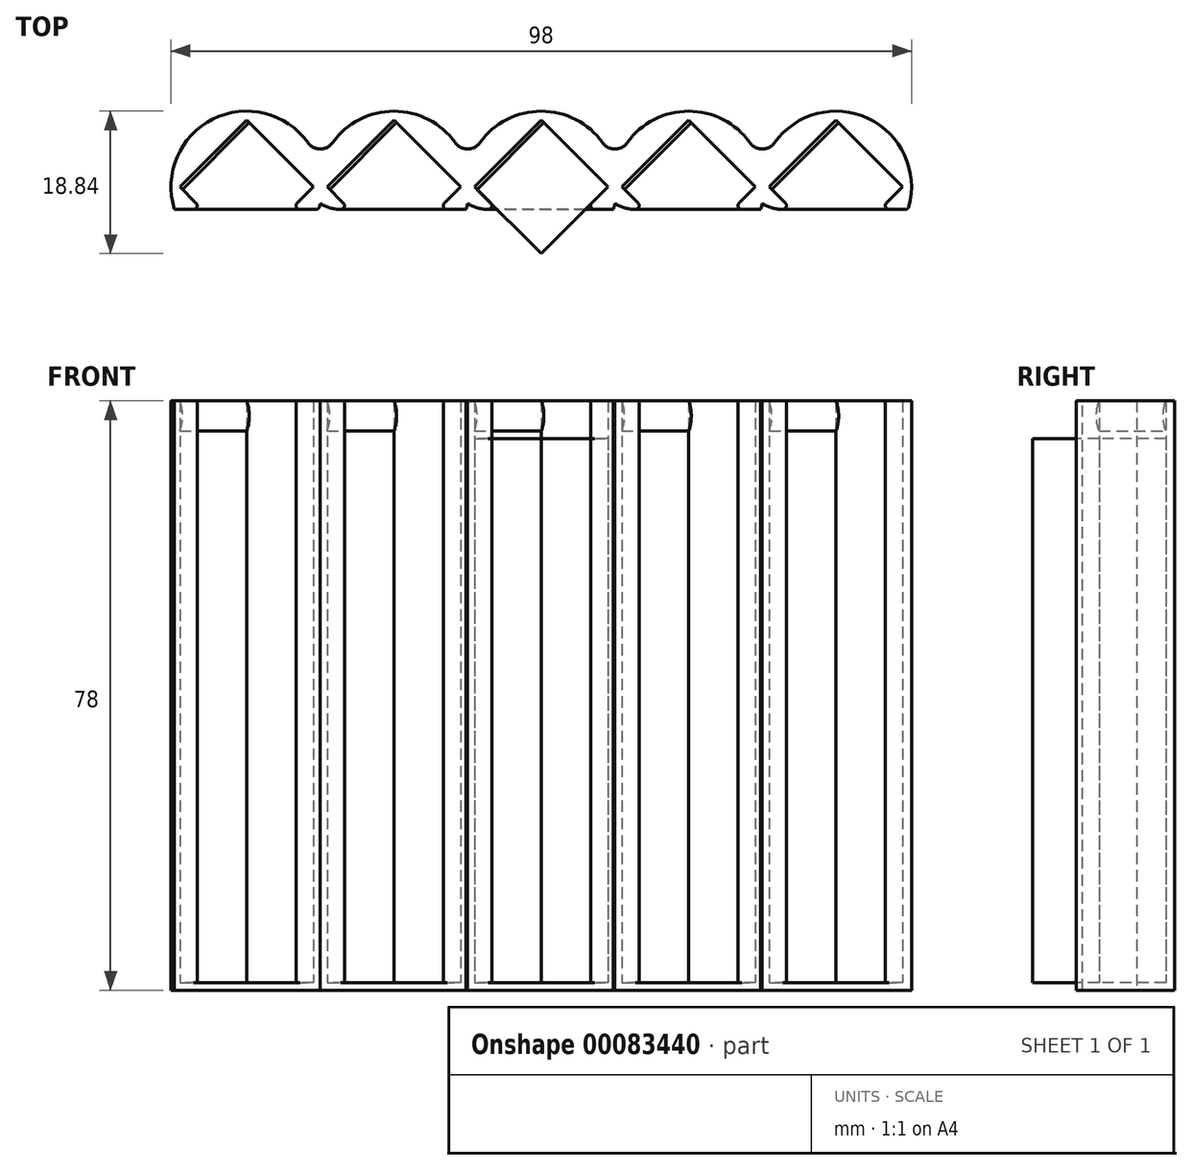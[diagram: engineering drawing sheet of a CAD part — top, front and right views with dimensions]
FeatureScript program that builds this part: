
annotation { "Feature Type Name" : "Feature", "Feature Type Description" : "" }
export const myFeature = defineFeature(function(context is Context, id is Id, definition is map)
    precondition{}
    {
        {
            assignVariable(context, id + "F0", {"name" : "dieSize", "anyValue" : 12.5});
        }
        {
            var Q0;
            Q0=qCreatedBy(makeId("Top.planeOp"),FACE);
            var sketch = newSketch(context, id + "F1", { "sketchPlane" : qUnion([Q0])});
            skCircle(sketch, "E0", {"center": v(0, 0) * mm, "radius": 10 * mm});
            skLineSegment(sketch, "E1", {"start": v(0, 0) * mm, "end": v(0, 26.13) * mm, "construction": true});
            skLineSegment(sketch, "E2", {"start": v(0, 8.84) * mm, "end": v(-8.84, 0) * mm});
            skLineSegment(sketch, "E3", {"start": v(0, 8.84) * mm, "end": v(8.84, 0) * mm});
            skLineSegment(sketch, "E4", {"start": v(8.84, 0) * mm, "end": v(0, -8.84) * mm});
            skLineSegment(sketch, "E5", {"start": v(-8.84, 0) * mm, "end": v(0, -8.84) * mm});
            skLineSegment(sketch, "E6", {"start": v(0, 0) * mm, "end": v(18.44, -18.44) * mm, "construction": true});
            skLineSegment(sketch, "E7", {"start": v(0, 0) * mm, "end": v(-23.78, 0) * mm, "construction": true});
            skLineSegment(sketch, "E8.1.0.0", {"start": v(28.34, 0) * mm, "end": v(19.5, -8.84) * mm});
            skLineSegment(sketch, "E8.1.0.1", {"start": v(19.5, 8.84) * mm, "end": v(28.34, 0) * mm});
            skLineSegment(sketch, "E8.1.0.2", {"start": v(10.66, 0) * mm, "end": v(19.5, -8.84) * mm});
            skCircle(sketch, "E8.1.0.3", {"center": v(19.5, 0) * mm, "radius": 10 * mm});
            skLineSegment(sketch, "E8.1.0.4", {"start": v(19.5, 8.84) * mm, "end": v(10.66, 0) * mm});
            skLineSegment(sketch, "E8.2.0.0", {"start": v(47.84, 0) * mm, "end": v(39, -8.84) * mm});
            skLineSegment(sketch, "E8.2.0.1", {"start": v(39, 8.84) * mm, "end": v(47.84, 0) * mm});
            skLineSegment(sketch, "E8.2.0.2", {"start": v(30.16, 0) * mm, "end": v(39, -8.84) * mm});
            skCircle(sketch, "E8.2.0.3", {"center": v(39, 0) * mm, "radius": 10 * mm});
            skLineSegment(sketch, "E8.2.0.4", {"start": v(39, 8.84) * mm, "end": v(30.16, 0) * mm});
            skLineSegment(sketch, "E8.3.0.0", {"start": v(67.34, 0) * mm, "end": v(58.5, -8.84) * mm});
            skLineSegment(sketch, "E8.3.0.1", {"start": v(58.5, 8.84) * mm, "end": v(67.34, 0) * mm});
            skLineSegment(sketch, "E8.3.0.2", {"start": v(49.66, 0) * mm, "end": v(58.5, -8.84) * mm});
            skCircle(sketch, "E8.3.0.3", {"center": v(58.5, 0) * mm, "radius": 10 * mm});
            skLineSegment(sketch, "E8.3.0.4", {"start": v(58.5, 8.84) * mm, "end": v(49.66, 0) * mm});
            skLineSegment(sketch, "E8.4.0.0", {"start": v(86.84, 0) * mm, "end": v(78, -8.84) * mm});
            skLineSegment(sketch, "E8.4.0.1", {"start": v(78, 8.84) * mm, "end": v(86.84, 0) * mm});
            skLineSegment(sketch, "E8.4.0.2", {"start": v(69.16, 0) * mm, "end": v(78, -8.84) * mm});
            skCircle(sketch, "E8.4.0.3", {"center": v(78, 0) * mm, "radius": 10 * mm});
            skLineSegment(sketch, "E8.4.0.4", {"start": v(78, 8.84) * mm, "end": v(69.16, 0) * mm});
            skLineSegment(sketch, "E8.direction1", {"start": v(0, -8.84) * mm, "end": v(19.5, -8.84) * mm, "construction": true});
            skSolve(sketch);
        }
        {
            var Q0;
            Q0=makeQuery(id+"F1.imprint","IMPRINT",FACE,{"disambiguationData":[TD([[makeQuery(id+"F1.imprint","IMPRINT",EDGE,{"derivedFrom":sQuery(id+"F1.wireOp",EDGE,"E0")}),1.0]])]});
            var Q1;
            Q1=makeQuery(id+"F1.imprint","IMPRINT",FACE,{"disambiguationData":[TD([[makeQuery(id+"F1.imprint","IMPRINT",EDGE,{"derivedFrom":sQuery(id+"F1.wireOp",EDGE,"E8.1.0.0")}),1.0]])]});
            var Q2;
            Q2=makeQuery(id+"F1.imprint","IMPRINT",FACE,{"disambiguationData":[TD([[makeQuery(id+"F1.imprint","IMPRINT",EDGE,{"derivedFrom":sQuery(id+"F1.wireOp",EDGE,"E2")}),1.0]])]});
            var Q3;
            Q3=makeQuery(id+"F1.imprint","IMPRINT",FACE,{"disambiguationData":[TD([[makeQuery(id+"F1.imprint","IMPRINT",EDGE,{"derivedFrom":sQuery(id+"F1.wireOp",EDGE,"E8.1.0.0")}),-1.0]])]});
            var Q4;
            Q4=makeQuery(id+"F1.imprint","IMPRINT",FACE,{"disambiguationData":[TD([[makeQuery(id+"F1.imprint","IMPRINT",EDGE,{"derivedFrom":sQuery(id+"F1.wireOp",EDGE,"E8.2.0.0")}),-1.0]])]});
            var Q5;
            Q5=makeQuery(id+"F1.imprint","IMPRINT",FACE,{"disambiguationData":[TD([[makeQuery(id+"F1.imprint","IMPRINT",EDGE,{"derivedFrom":sQuery(id+"F1.wireOp",EDGE,"E8.3.0.0")}),-1.0]])]});
            var Q6;
            Q6=makeQuery(id+"F1.imprint","IMPRINT",FACE,{"disambiguationData":[TD([[makeQuery(id+"F1.imprint","IMPRINT",EDGE,{"derivedFrom":sQuery(id+"F1.wireOp",EDGE,"E8.4.0.0")}),-1.0]])]});
            var Q7;
            Q7=makeQuery(id+"F1.imprint","IMPRINT",FACE,{"disambiguationData":[TD([[makeQuery(id+"F1.imprint","IMPRINT",EDGE,{"derivedFrom":sQuery(id+"F1.wireOp",EDGE,"E2")}),-1.0]])]});
            var Q8;
            {var subQ0=sQuery(id+"F1.wireOp",EDGE,"E8.2.0.3");var subQ1=sQuery(id+"F1.wireOp",EDGE,"E8.1.0.3");var subQ2=makeQuery(id+"F1.imprint","INTERSECT",VERTEX,{"disambiguationData":[OD(0.0)],"derivedFrom":[subQ1,subQ0]});Q8=makeQuery(id+"F1.imprint","IMPRINT",FACE,{"disambiguationData":[TD([[makeQuery(id+"F1.imprint","IMPRINT",EDGE,{"disambiguationData":[TD([[subQ2,1.0]])],"derivedFrom":subQ1}),1.0]])]});}
            var Q9;
            Q9=makeQuery(id+"F1.imprint","IMPRINT",FACE,{"disambiguationData":[TD([[makeQuery(id+"F1.imprint","IMPRINT",EDGE,{"derivedFrom":sQuery(id+"F1.wireOp",EDGE,"E8.2.0.0")}),1.0]])]});
            var Q10;
            {var subQ0=sQuery(id+"F1.wireOp",EDGE,"E8.3.0.3");var subQ1=sQuery(id+"F1.wireOp",EDGE,"E8.2.0.3");var subQ2=makeQuery(id+"F1.imprint","INTERSECT",VERTEX,{"disambiguationData":[OD(0.0)],"derivedFrom":[subQ1,subQ0]});Q10=makeQuery(id+"F1.imprint","IMPRINT",FACE,{"disambiguationData":[TD([[makeQuery(id+"F1.imprint","IMPRINT",EDGE,{"disambiguationData":[TD([[subQ2,1.0]])],"derivedFrom":subQ1}),1.0]])]});}
            var Q11;
            Q11=makeQuery(id+"F1.imprint","IMPRINT",FACE,{"disambiguationData":[TD([[makeQuery(id+"F1.imprint","IMPRINT",EDGE,{"derivedFrom":sQuery(id+"F1.wireOp",EDGE,"E8.4.0.0")}),1.0]])]});
            var Q12;
            {var subQ0=sQuery(id+"F1.wireOp",EDGE,"E8.4.0.3");var subQ1=sQuery(id+"F1.wireOp",EDGE,"E8.3.0.3");var subQ2=makeQuery(id+"F1.imprint","INTERSECT",VERTEX,{"disambiguationData":[OD(0.0)],"derivedFrom":[subQ1,subQ0]});Q12=makeQuery(id+"F1.imprint","IMPRINT",FACE,{"disambiguationData":[TD([[makeQuery(id+"F1.imprint","IMPRINT",EDGE,{"disambiguationData":[TD([[subQ2,1.0]])],"derivedFrom":subQ1}),1.0]])]});}
            var Q13;
            Q13=makeQuery(id+"F1.imprint","IMPRINT",FACE,{"disambiguationData":[TD([[makeQuery(id+"F1.imprint","IMPRINT",EDGE,{"derivedFrom":sQuery(id+"F1.wireOp",EDGE,"E8.3.0.0")}),1.0]])]});
            extrude(context, id + "F2", {"entities" : qUnion([Q0, Q1, Q2, Q3, Q4, Q5, Q6, Q7, Q8, Q9, Q10, Q11, Q12, Q13]), "oppositeDirection" : true, "depth" : 1 * mm});
        }
        {
            var Q0;
            Q0=makeQuery(id+"F1.imprint","IMPRINT",FACE,{"disambiguationData":[TD([[makeQuery(id+"F1.imprint","IMPRINT",EDGE,{"derivedFrom":sQuery(id+"F1.wireOp",EDGE,"E8.2.0.0")}),1.0]])]});
            var Q1;
            {var subQ0=sQuery(id+"F1.wireOp",EDGE,"E8.3.0.3");var subQ1=sQuery(id+"F1.wireOp",EDGE,"E8.2.0.3");var subQ2=makeQuery(id+"F1.imprint","INTERSECT",VERTEX,{"disambiguationData":[OD(0.0)],"derivedFrom":[subQ1,subQ0]});Q1=makeQuery(id+"F1.imprint","IMPRINT",FACE,{"disambiguationData":[TD([[makeQuery(id+"F1.imprint","IMPRINT",EDGE,{"disambiguationData":[TD([[subQ2,1.0]])],"derivedFrom":subQ1}),1.0]])]});}
            var Q2;
            {var subQ0=sQuery(id+"F1.wireOp",EDGE,"E8.2.0.3");var subQ1=sQuery(id+"F1.wireOp",EDGE,"E8.1.0.3");var subQ2=makeQuery(id+"F1.imprint","INTERSECT",VERTEX,{"disambiguationData":[OD(0.0)],"derivedFrom":[subQ1,subQ0]});Q2=makeQuery(id+"F1.imprint","IMPRINT",FACE,{"disambiguationData":[TD([[makeQuery(id+"F1.imprint","IMPRINT",EDGE,{"disambiguationData":[TD([[subQ2,1.0]])],"derivedFrom":subQ1}),1.0]])]});}
            var Q3;
            {var subQ0=sQuery(id+"F1.wireOp",EDGE,"E8.1.0.3");var subQ1=sQuery(id+"F1.wireOp",EDGE,"E0");var subQ2=makeQuery(id+"F1.imprint","INTERSECT",VERTEX,{"disambiguationData":[OD(0.0)],"derivedFrom":[subQ1,subQ0]});Q3=makeQuery(id+"F1.imprint","IMPRINT",FACE,{"disambiguationData":[TD([[makeQuery(id+"F1.imprint","IMPRINT",EDGE,{"disambiguationData":[TD([[subQ2,1.0]])],"derivedFrom":subQ1}),1.0]])]});}
            var Q4;
            Q4=makeQuery(id+"F1.imprint","IMPRINT",FACE,{"disambiguationData":[TD([[makeQuery(id+"F1.imprint","IMPRINT",EDGE,{"derivedFrom":sQuery(id+"F1.wireOp",EDGE,"E8.1.0.0")}),1.0]])]});
            var Q5;
            Q5=makeQuery(id+"F1.imprint","IMPRINT",FACE,{"disambiguationData":[TD([[makeQuery(id+"F1.imprint","IMPRINT",EDGE,{"derivedFrom":sQuery(id+"F1.wireOp",EDGE,"E2")}),-1.0]])]});
            var Q6;
            Q6=makeQuery(id+"F1.imprint","IMPRINT",FACE,{"disambiguationData":[TD([[makeQuery(id+"F1.imprint","IMPRINT",EDGE,{"derivedFrom":sQuery(id+"F1.wireOp",EDGE,"E8.3.0.0")}),1.0]])]});
            var Q7;
            {var subQ0=sQuery(id+"F1.wireOp",EDGE,"E8.4.0.3");var subQ1=sQuery(id+"F1.wireOp",EDGE,"E8.3.0.3");var subQ2=makeQuery(id+"F1.imprint","INTERSECT",VERTEX,{"disambiguationData":[OD(0.0)],"derivedFrom":[subQ1,subQ0]});Q7=makeQuery(id+"F1.imprint","IMPRINT",FACE,{"disambiguationData":[TD([[makeQuery(id+"F1.imprint","IMPRINT",EDGE,{"disambiguationData":[TD([[subQ2,1.0]])],"derivedFrom":subQ1}),1.0]])]});}
            var Q8;
            Q8=makeQuery(id+"F1.imprint","IMPRINT",FACE,{"disambiguationData":[TD([[makeQuery(id+"F1.imprint","IMPRINT",EDGE,{"derivedFrom":sQuery(id+"F1.wireOp",EDGE,"E8.4.0.0")}),1.0]])]});
            extrude(context, id + "F3", {"entities" : qUnion([Q0, Q1, Q2, Q3, Q4, Q5, Q6, Q7, Q8]), "operationType" : NewBodyOperationType.ADD, "depth" : (getVariable(context, 'dieSize') * 6 + 2) * mm});
        }
        {
            var Q0;
            Q0=makeQuery(id+"F3.opExtrude","CAP_FACE",FACE,{"disambiguationData":[OSD([sQuery(id+"F1.wireOp",EDGE,"E0"),sQuery(id+"F1.wireOp",EDGE,"E2"),sQuery(id+"F1.wireOp",EDGE,"E3"),sQuery(id+"F1.wireOp",EDGE,"E4"),sQuery(id+"F1.wireOp",EDGE,"E5"),sQuery(id+"F1.wireOp",EDGE,"E8.1.0.0"),sQuery(id+"F1.wireOp",EDGE,"E8.1.0.1"),sQuery(id+"F1.wireOp",EDGE,"E8.1.0.2"),sQuery(id+"F1.wireOp",EDGE,"E8.1.0.3"),sQuery(id+"F1.wireOp",EDGE,"E8.1.0.4"),sQuery(id+"F1.wireOp",EDGE,"E8.2.0.0"),sQuery(id+"F1.wireOp",EDGE,"E8.2.0.1"),sQuery(id+"F1.wireOp",EDGE,"E8.2.0.2"),sQuery(id+"F1.wireOp",EDGE,"E8.2.0.3"),sQuery(id+"F1.wireOp",EDGE,"E8.2.0.4"),sQuery(id+"F1.wireOp",EDGE,"E8.3.0.0"),sQuery(id+"F1.wireOp",EDGE,"E8.3.0.1"),sQuery(id+"F1.wireOp",EDGE,"E8.3.0.2"),sQuery(id+"F1.wireOp",EDGE,"E8.3.0.3"),sQuery(id+"F1.wireOp",EDGE,"E8.3.0.4"),sQuery(id+"F1.wireOp",EDGE,"E8.4.0.0"),sQuery(id+"F1.wireOp",EDGE,"E8.4.0.1"),sQuery(id+"F1.wireOp",EDGE,"E8.4.0.2"),sQuery(id+"F1.wireOp",EDGE,"E8.4.0.3"),sQuery(id+"F1.wireOp",EDGE,"E8.4.0.4")])],"isStart":false});
            var sketch = newSketch(context, id + "F4", { "sketchPlane" : qUnion([Q0])});
            skLineSegment(sketch, "E9.bottom", {"start": v(90.34, -3) * mm, "end": v(-15.54, -3) * mm});
            skLineSegment(sketch, "E9.top", {"start": v(90.34, -14.24) * mm, "end": v(-15.54, -14.24) * mm});
            skLineSegment(sketch, "E9.left", {"start": v(90.34, -3) * mm, "end": v(90.34, -14.24) * mm});
            skLineSegment(sketch, "E9.right", {"start": v(-15.54, -3) * mm, "end": v(-15.54, -14.24) * mm});
            skSolve(sketch);
        }
        {
            var Q0;
            {var subQ3=sQuery(id+"F4.wireOp",EDGE,"E9.bottom");var subQ5=makeQuery(id+"F3.opExtrude","CAP_EDGE",EDGE,{"disambiguationData":[OSD([sQuery(id+"F1.wireOp",EDGE,"E0")])],"isStart":false});var subQ7=makeQuery(id+"F4.imprint","INTERSECT",VERTEX,{"disambiguationData":[OD(1.0)],"derivedFrom":[subQ5,subQ3]});Q0=makeQuery(id+"F4.imprint","IMPRINT",FACE,{"disambiguationData":[TD([[makeQuery(id+"F4.imprint","IMPRINT",EDGE,{"disambiguationData":[TD([[subQ7,-1.0]])],"derivedFrom":subQ3}),1.0]])]});}
            var Q1;
            {var subQ0=sQuery(id+"F4.wireOp",EDGE,"E9.bottom");var subQ1=makeQuery(id+"F3.opExtrude","CAP_EDGE",EDGE,{"disambiguationData":[OSD([sQuery(id+"F1.wireOp",EDGE,"E4")])],"isStart":false});var subQ2=makeQuery(id+"F4.imprint","INTERSECT",VERTEX,{"derivedFrom":[subQ1,subQ0]});Q1=makeQuery(id+"F4.imprint","IMPRINT",FACE,{"disambiguationData":[TD([[makeQuery(id+"F4.imprint","IMPRINT",EDGE,{"disambiguationData":[TD([[subQ2,-1.0]])],"derivedFrom":subQ0}),1.0]])]});}
            var Q2;
            {var subQ0=makeQuery(id+"F3.opExtrude","CAP_EDGE",EDGE,{"disambiguationData":[OSD([sQuery(id+"F1.wireOp",EDGE,"E8.1.0.2")])],"isStart":false});var subQ1=makeQuery(id+"F3.opExtrude","CAP_EDGE",EDGE,{"disambiguationData":[OSD([sQuery(id+"F1.wireOp",EDGE,"E8.1.0.0")])],"isStart":false});var subQ2=makeQuery(id+"F4.imprint","INTERSECT",VERTEX,{"derivedFrom":[subQ1,subQ0]});Q2=makeQuery(id+"F4.imprint","IMPRINT",FACE,{"disambiguationData":[TD([[makeQuery(id+"F4.imprint","IMPRINT",EDGE,{"disambiguationData":[TD([[subQ2,1.0]])],"derivedFrom":subQ1}),1.0]])]});}
            var Q3;
            {var subQ0=sQuery(id+"F4.wireOp",EDGE,"E9.bottom");var subQ1=makeQuery(id+"F3.opExtrude","CAP_EDGE",EDGE,{"disambiguationData":[OSD([sQuery(id+"F1.wireOp",EDGE,"E8.1.0.0")])],"isStart":false});var subQ2=makeQuery(id+"F4.imprint","INTERSECT",VERTEX,{"derivedFrom":[subQ1,subQ0]});Q3=makeQuery(id+"F4.imprint","IMPRINT",FACE,{"disambiguationData":[TD([[makeQuery(id+"F4.imprint","IMPRINT",EDGE,{"disambiguationData":[TD([[subQ2,-1.0]])],"derivedFrom":subQ0}),1.0]])]});}
            var Q4;
            {var subQ0=makeQuery(id+"F3.opExtrude","CAP_EDGE",EDGE,{"disambiguationData":[OSD([sQuery(id+"F1.wireOp",EDGE,"E8.2.0.2")])],"isStart":false});var subQ1=makeQuery(id+"F3.opExtrude","CAP_EDGE",EDGE,{"disambiguationData":[OSD([sQuery(id+"F1.wireOp",EDGE,"E8.2.0.0")])],"isStart":false});var subQ2=makeQuery(id+"F4.imprint","INTERSECT",VERTEX,{"derivedFrom":[subQ1,subQ0]});Q4=makeQuery(id+"F4.imprint","IMPRINT",FACE,{"disambiguationData":[TD([[makeQuery(id+"F4.imprint","IMPRINT",EDGE,{"disambiguationData":[TD([[subQ2,1.0]])],"derivedFrom":subQ1}),1.0]])]});}
            var Q5;
            {var subQ0=sQuery(id+"F4.wireOp",EDGE,"E9.bottom");var subQ1=makeQuery(id+"F3.opExtrude","CAP_EDGE",EDGE,{"disambiguationData":[OSD([sQuery(id+"F1.wireOp",EDGE,"E8.2.0.0")])],"isStart":false});var subQ2=makeQuery(id+"F4.imprint","INTERSECT",VERTEX,{"derivedFrom":[subQ1,subQ0]});Q5=makeQuery(id+"F4.imprint","IMPRINT",FACE,{"disambiguationData":[TD([[makeQuery(id+"F4.imprint","IMPRINT",EDGE,{"disambiguationData":[TD([[subQ2,-1.0]])],"derivedFrom":subQ0}),1.0]])]});}
            var Q6;
            {var subQ0=makeQuery(id+"F3.opExtrude","CAP_EDGE",EDGE,{"disambiguationData":[OSD([sQuery(id+"F1.wireOp",EDGE,"E8.3.0.2")])],"isStart":false});var subQ1=makeQuery(id+"F3.opExtrude","CAP_EDGE",EDGE,{"disambiguationData":[OSD([sQuery(id+"F1.wireOp",EDGE,"E8.3.0.0")])],"isStart":false});var subQ2=makeQuery(id+"F4.imprint","INTERSECT",VERTEX,{"derivedFrom":[subQ1,subQ0]});Q6=makeQuery(id+"F4.imprint","IMPRINT",FACE,{"disambiguationData":[TD([[makeQuery(id+"F4.imprint","IMPRINT",EDGE,{"disambiguationData":[TD([[subQ2,1.0]])],"derivedFrom":subQ1}),1.0]])]});}
            var Q7;
            {var subQ0=sQuery(id+"F4.wireOp",EDGE,"E9.bottom");var subQ1=makeQuery(id+"F3.opExtrude","CAP_EDGE",EDGE,{"disambiguationData":[OSD([sQuery(id+"F1.wireOp",EDGE,"E8.3.0.0")])],"isStart":false});var subQ2=makeQuery(id+"F4.imprint","INTERSECT",VERTEX,{"derivedFrom":[subQ1,subQ0]});Q7=makeQuery(id+"F4.imprint","IMPRINT",FACE,{"disambiguationData":[TD([[makeQuery(id+"F4.imprint","IMPRINT",EDGE,{"disambiguationData":[TD([[subQ2,-1.0]])],"derivedFrom":subQ0}),1.0]])]});}
            var Q8;
            {var subQ3=sQuery(id+"F4.wireOp",EDGE,"E9.bottom");var subQ6=makeQuery(id+"F3.opExtrude","CAP_EDGE",EDGE,{"disambiguationData":[OSD([sQuery(id+"F1.wireOp",EDGE,"E8.4.0.3")])],"isStart":false});var subQ8=makeQuery(id+"F4.imprint","INTERSECT",VERTEX,{"disambiguationData":[OD(0.0)],"derivedFrom":[subQ6,subQ3]});Q8=makeQuery(id+"F4.imprint","IMPRINT",FACE,{"disambiguationData":[TD([[makeQuery(id+"F4.imprint","IMPRINT",EDGE,{"disambiguationData":[TD([[subQ8,-1.0]])],"derivedFrom":subQ3}),1.0]])]});}
            var Q9;
            {var subQ0=sQuery(id+"F4.wireOp",EDGE,"E9.bottom");var subQ1=makeQuery(id+"F3.opExtrude","CAP_EDGE",EDGE,{"disambiguationData":[OSD([sQuery(id+"F1.wireOp",EDGE,"E8.4.0.0")])],"isStart":false});var subQ2=makeQuery(id+"F4.imprint","INTERSECT",VERTEX,{"derivedFrom":[subQ1,subQ0]});Q9=makeQuery(id+"F4.imprint","IMPRINT",FACE,{"disambiguationData":[TD([[makeQuery(id+"F4.imprint","IMPRINT",EDGE,{"disambiguationData":[TD([[subQ2,-1.0]])],"derivedFrom":subQ0}),1.0]])]});}
            var Q10;
            Q10=makeQuery(id+"F2.opExtrude","CAP_FACE",FACE,{"disambiguationData":[OSD([sQuery(id+"F1.wireOp",EDGE,"E0"),sQuery(id+"F1.wireOp",EDGE,"E8.1.0.3"),sQuery(id+"F1.wireOp",EDGE,"E8.2.0.3"),sQuery(id+"F1.wireOp",EDGE,"E8.3.0.3"),sQuery(id+"F1.wireOp",EDGE,"E8.4.0.3")])],"isStart":false});
            extrude(context, id + "F5", {"entities" : qUnion([Q0, Q1, Q2, Q3, Q4, Q5, Q6, Q7, Q8, Q9]), "operationType" : NewBodyOperationType.REMOVE, "endBound" : BoundingType.UP_TO_SURFACE, "oppositeDirection" : true, "endBoundEntityFace" : qUnion([Q10]), "depth" : 25 * mm});
        }
        {
            var Q0;
            {var subQ0=sQuery(id+"F1.wireOp",EDGE,"E8.4.0.3");var subQ1=sQuery(id+"F1.wireOp",EDGE,"E8.3.0.3");var subQ2=makeQuery(id+"F1.imprint","INTERSECT",VERTEX,{"disambiguationData":[OD(0.0)],"derivedFrom":[subQ1,subQ0]});Q0=makeQuery(id+"F3.boolean.opBoolean","MERGE",EDGE,{"derivedFrom":[makeQuery(id+"F2.opExtrude","SWEPT_EDGE",EDGE,{"disambiguationData":[OSD([subQ1,subQ0]),TDD([subQ2])]}),makeQuery(id+"F3.opExtrude","SWEPT_EDGE",EDGE,{"disambiguationData":[OSD([subQ1,subQ0]),TDD([subQ2])]})]});}
            var Q1;
            {var subQ0=sQuery(id+"F1.wireOp",EDGE,"E8.3.0.3");var subQ1=sQuery(id+"F1.wireOp",EDGE,"E8.2.0.3");var subQ2=makeQuery(id+"F1.imprint","INTERSECT",VERTEX,{"disambiguationData":[OD(0.0)],"derivedFrom":[subQ1,subQ0]});Q1=makeQuery(id+"F3.boolean.opBoolean","MERGE",EDGE,{"derivedFrom":[makeQuery(id+"F2.opExtrude","SWEPT_EDGE",EDGE,{"disambiguationData":[OSD([subQ1,subQ0]),TDD([subQ2])]}),makeQuery(id+"F3.opExtrude","SWEPT_EDGE",EDGE,{"disambiguationData":[OSD([subQ1,subQ0]),TDD([subQ2])]})]});}
            var Q2;
            {var subQ0=sQuery(id+"F1.wireOp",EDGE,"E8.2.0.3");var subQ1=sQuery(id+"F1.wireOp",EDGE,"E8.1.0.3");var subQ2=makeQuery(id+"F1.imprint","INTERSECT",VERTEX,{"disambiguationData":[OD(0.0)],"derivedFrom":[subQ1,subQ0]});Q2=makeQuery(id+"F3.boolean.opBoolean","MERGE",EDGE,{"derivedFrom":[makeQuery(id+"F2.opExtrude","SWEPT_EDGE",EDGE,{"disambiguationData":[OSD([subQ1,subQ0]),TDD([subQ2])]}),makeQuery(id+"F3.opExtrude","SWEPT_EDGE",EDGE,{"disambiguationData":[OSD([subQ1,subQ0]),TDD([subQ2])]})]});}
            var Q3;
            {var subQ0=sQuery(id+"F1.wireOp",EDGE,"E8.1.0.3");var subQ1=sQuery(id+"F1.wireOp",EDGE,"E0");var subQ2=makeQuery(id+"F1.imprint","INTERSECT",VERTEX,{"disambiguationData":[OD(0.0)],"derivedFrom":[subQ1,subQ0]});Q3=makeQuery(id+"F3.boolean.opBoolean","MERGE",EDGE,{"derivedFrom":[makeQuery(id+"F2.opExtrude","SWEPT_EDGE",EDGE,{"disambiguationData":[OSD([subQ1,subQ0]),TDD([subQ2])]}),makeQuery(id+"F3.opExtrude","SWEPT_EDGE",EDGE,{"disambiguationData":[OSD([subQ1,subQ0]),TDD([subQ2])]})]});}
            fillet(context, id + "F6", {"entities" : qUnion([Q0, Q1, Q2, Q3]), "radius" : 2 * mm, "tangentPropagation" : true, "allowEdgeOverflow" : false});
        }
        {
            var Q0;
            Q0=makeQuery(id+"F1.imprint","IMPRINT",FACE,{"disambiguationData":[TD([[makeQuery(id+"F1.imprint","IMPRINT",EDGE,{"derivedFrom":sQuery(id+"F1.wireOp",EDGE,"E8.2.0.0")}),-1.0]])]});
            extrude(context, id + "F7", {"entities" : qUnion([Q0]), "depth" : (12 * 6) * mm});
        }
        {
            var Q0;
            Q0=makeQuery(id+"F5.boolean.opBoolean","INTERSECT",EDGE,{"derivedFrom":[makeQuery(id+"F3.opExtrude","SWEPT_FACE",FACE,{"disambiguationData":[OSD([sQuery(id+"F1.wireOp",EDGE,"E8.2.0.0")])]}),makeQuery(id+"F5.opExtrude","SWEPT_FACE",FACE,{"disambiguationData":[OSD([sQuery(id+"F4.wireOp",EDGE,"E9.bottom")])]})]});
            var Q1;
            Q1=makeQuery(id+"F5.boolean.opBoolean","INTERSECT",EDGE,{"derivedFrom":[makeQuery(id+"F3.opExtrude","SWEPT_FACE",FACE,{"disambiguationData":[OSD([sQuery(id+"F1.wireOp",EDGE,"E8.3.0.2")])]}),makeQuery(id+"F5.opExtrude","SWEPT_FACE",FACE,{"disambiguationData":[OSD([sQuery(id+"F4.wireOp",EDGE,"E9.bottom")])]})]});
            var Q2;
            Q2=makeQuery(id+"F5.boolean.opBoolean","INTERSECT",EDGE,{"derivedFrom":[makeQuery(id+"F3.opExtrude","SWEPT_FACE",FACE,{"disambiguationData":[OSD([sQuery(id+"F1.wireOp",EDGE,"E8.4.0.0")])]}),makeQuery(id+"F5.opExtrude","SWEPT_FACE",FACE,{"disambiguationData":[OSD([sQuery(id+"F4.wireOp",EDGE,"E9.bottom")])]})]});
            var Q3;
            {var subQ0=sQuery(id+"F1.wireOp",EDGE,"E8.4.0.3");Q3=makeQuery(id+"F5.boolean.opBoolean","INTERSECT",EDGE,{"derivedFrom":[makeQuery(id+"F3.boolean.opBoolean","MERGE",FACE,{"derivedFrom":[makeQuery(id+"F2.opExtrude","SWEPT_FACE",FACE,{"disambiguationData":[OSD([subQ0])]}),makeQuery(id+"F3.opExtrude","SWEPT_FACE",FACE,{"disambiguationData":[OSD([subQ0])]})]}),makeQuery(id+"F5.opExtrude","SWEPT_FACE",FACE,{"disambiguationData":[OSD([sQuery(id+"F4.wireOp",EDGE,"E9.bottom")])]})]});}
            var Q4;
            Q4=makeQuery(id+"F5.boolean.opBoolean","INTERSECT",EDGE,{"derivedFrom":[makeQuery(id+"F3.opExtrude","SWEPT_FACE",FACE,{"disambiguationData":[OSD([sQuery(id+"F1.wireOp",EDGE,"E8.4.0.2")])]}),makeQuery(id+"F5.opExtrude","SWEPT_FACE",FACE,{"disambiguationData":[OSD([sQuery(id+"F4.wireOp",EDGE,"E9.bottom")])]})]});
            var Q5;
            Q5=makeQuery(id+"F5.boolean.opBoolean","INTERSECT",EDGE,{"derivedFrom":[makeQuery(id+"F3.opExtrude","SWEPT_FACE",FACE,{"disambiguationData":[OSD([sQuery(id+"F1.wireOp",EDGE,"E8.3.0.0")])]}),makeQuery(id+"F5.opExtrude","SWEPT_FACE",FACE,{"disambiguationData":[OSD([sQuery(id+"F4.wireOp",EDGE,"E9.bottom")])]})]});
            var Q6;
            Q6=makeQuery(id+"F5.boolean.opBoolean","INTERSECT",EDGE,{"derivedFrom":[makeQuery(id+"F3.opExtrude","SWEPT_FACE",FACE,{"disambiguationData":[OSD([sQuery(id+"F1.wireOp",EDGE,"E8.2.0.2")])]}),makeQuery(id+"F5.opExtrude","SWEPT_FACE",FACE,{"disambiguationData":[OSD([sQuery(id+"F4.wireOp",EDGE,"E9.bottom")])]})]});
            var Q7;
            Q7=makeQuery(id+"F5.boolean.opBoolean","INTERSECT",EDGE,{"derivedFrom":[makeQuery(id+"F3.opExtrude","SWEPT_FACE",FACE,{"disambiguationData":[OSD([sQuery(id+"F1.wireOp",EDGE,"E8.1.0.0")])]}),makeQuery(id+"F5.opExtrude","SWEPT_FACE",FACE,{"disambiguationData":[OSD([sQuery(id+"F4.wireOp",EDGE,"E9.bottom")])]})]});
            var Q8;
            Q8=makeQuery(id+"F5.boolean.opBoolean","INTERSECT",EDGE,{"derivedFrom":[makeQuery(id+"F3.opExtrude","SWEPT_FACE",FACE,{"disambiguationData":[OSD([sQuery(id+"F1.wireOp",EDGE,"E4")])]}),makeQuery(id+"F5.opExtrude","SWEPT_FACE",FACE,{"disambiguationData":[OSD([sQuery(id+"F4.wireOp",EDGE,"E9.bottom")])]})]});
            var Q9;
            Q9=makeQuery(id+"F5.boolean.opBoolean","INTERSECT",EDGE,{"derivedFrom":[makeQuery(id+"F3.opExtrude","SWEPT_FACE",FACE,{"disambiguationData":[OSD([sQuery(id+"F1.wireOp",EDGE,"E8.1.0.2")])]}),makeQuery(id+"F5.opExtrude","SWEPT_FACE",FACE,{"disambiguationData":[OSD([sQuery(id+"F4.wireOp",EDGE,"E9.bottom")])]})]});
            var Q10;
            Q10=makeQuery(id+"F5.boolean.opBoolean","INTERSECT",EDGE,{"derivedFrom":[makeQuery(id+"F3.opExtrude","SWEPT_FACE",FACE,{"disambiguationData":[OSD([sQuery(id+"F1.wireOp",EDGE,"E5")])]}),makeQuery(id+"F5.opExtrude","SWEPT_FACE",FACE,{"disambiguationData":[OSD([sQuery(id+"F4.wireOp",EDGE,"E9.bottom")])]})]});
            var Q11;
            {var subQ0=sQuery(id+"F1.wireOp",EDGE,"E0");Q11=makeQuery(id+"F5.boolean.opBoolean","INTERSECT",EDGE,{"derivedFrom":[makeQuery(id+"F3.boolean.opBoolean","MERGE",FACE,{"derivedFrom":[makeQuery(id+"F2.opExtrude","SWEPT_FACE",FACE,{"disambiguationData":[OSD([subQ0])]}),makeQuery(id+"F3.opExtrude","SWEPT_FACE",FACE,{"disambiguationData":[OSD([subQ0])]})]}),makeQuery(id+"F5.opExtrude","SWEPT_FACE",FACE,{"disambiguationData":[OSD([sQuery(id+"F4.wireOp",EDGE,"E9.bottom")])]})]});}
            fillet(context, id + "F8", {"entities" : qUnion([Q0, Q1, Q2, Q3, Q4, Q5, Q6, Q7, Q8, Q9, Q10, Q11]), "radius" : .5 * mm, "tangentPropagation" : true, "allowEdgeOverflow" : false});
        }
        {
            var Q0;
            Q0=makeQuery(id+"F3.opExtrude","SWEPT_FACE",FACE,{"disambiguationData":[OSD([sQuery(id+"F1.wireOp",EDGE,"E8.2.0.1")])]});
            var sketch = newSketch(context, id + "F9", { "sketchPlane" : qUnion([Q0])});
            skArc(sketch, "E10", {"start": v(21.33, 73) * mm, "mid": v(21.83, 75) * mm, "end": v(21.33, 77) * mm});
            skSolve(sketch);
        }
        {
            var Q0;
            Q0 = qSketchRegion(id + "F9", true);
            var Q1;
            {var subQ0=sQuery(id+"F9.wireOp",EDGE,"E10");Q1=makeQuery(id+"F9.imprint","IMPRINT",FACE,{"disambiguationData":[TD([[makeQuery(id+"F9.imprint","IMPRINT",EDGE,{"derivedFrom":subQ0}),1.0]])]});}
            extrude(context, id + "F10", {"entities" : qUnion([Q0, Q1]), "depth" : (getVariable(context, 'dieSize')) * mm});
        }
        {
            var Q0;
            Q0=makeQuery(id+"F10.opExtrude","SWEPT_BODY",BODY,{"disambiguationData":[OSD([sQuery(id+"F1.wireOp",EDGE,"E8.2.0.1"),sQuery(id+"F1.wireOp",EDGE,"E8.2.0.4"),sQuery(id+"F9.wireOp",EDGE,"E10")])]});
            var Q1;
            Q1=makeQuery(id+"F3.opExtrude","CAP_VERTEX",VERTEX,{"disambiguationData":[OSD([sQuery(id+"F1.wireOp",EDGE,"E8.2.0.1"),sQuery(id+"F1.wireOp",EDGE,"E8.2.0.4")])],"isStart":false});
            var Q2;
            Q2=makeQuery(id+"F3.opExtrude","CAP_VERTEX",VERTEX,{"disambiguationData":[OSD([sQuery(id+"F1.wireOp",EDGE,"E8.1.0.1"),sQuery(id+"F1.wireOp",EDGE,"E8.1.0.4")])],"isStart":false});
            transform(context, id + "F11", {"entities" : qUnion([Q0]), "transformType" : TransformType.TRANSLATION_ENTITY, "oppositeDirectionEntity" : false, "transformLine" : qUnion([Q1, Q2]), "makeCopy" : true});
        }
        {
            var Q0;
            Q0=makeQuery(id+"F10.opExtrude","SWEPT_BODY",BODY,{"disambiguationData":[OSD([sQuery(id+"F1.wireOp",EDGE,"E8.2.0.1"),sQuery(id+"F1.wireOp",EDGE,"E8.2.0.4"),sQuery(id+"F9.wireOp",EDGE,"E10")])]});
            var Q1;
            Q1=makeQuery(id+"F3.opExtrude","CAP_VERTEX",VERTEX,{"disambiguationData":[OSD([sQuery(id+"F1.wireOp",EDGE,"E8.2.0.1"),sQuery(id+"F1.wireOp",EDGE,"E8.2.0.4")])],"isStart":false});
            var Q2;
            Q2=makeQuery(id+"F3.opExtrude","CAP_VERTEX",VERTEX,{"disambiguationData":[OSD([sQuery(id+"F1.wireOp",EDGE,"E8.3.0.1"),sQuery(id+"F1.wireOp",EDGE,"E8.3.0.4")])],"isStart":false});
            transform(context, id + "F12", {"entities" : qUnion([Q0]), "transformType" : TransformType.TRANSLATION_ENTITY, "oppositeDirectionEntity" : false, "transformLine" : qUnion([Q1, Q2]), "makeCopy" : true});
        }
        {
            var Q0;
            Q0=makeQuery(id+"F11.opPattern","COPY",BODY,{"derivedFrom":makeQuery(id+"F10.opExtrude","SWEPT_BODY",BODY,{"disambiguationData":[OSD([sQuery(id+"F1.wireOp",EDGE,"E8.2.0.1"),sQuery(id+"F1.wireOp",EDGE,"E8.2.0.4"),sQuery(id+"F9.wireOp",EDGE,"E10")])]}),"instanceName":"1"});
            var Q1;
            Q1=makeQuery(id+"F3.opExtrude","CAP_VERTEX",VERTEX,{"disambiguationData":[OSD([sQuery(id+"F1.wireOp",EDGE,"E8.1.0.1"),sQuery(id+"F1.wireOp",EDGE,"E8.1.0.4")])],"isStart":false});
            var Q2;
            Q2=makeQuery(id+"F3.opExtrude","CAP_VERTEX",VERTEX,{"disambiguationData":[OSD([sQuery(id+"F1.wireOp",EDGE,"E2"),sQuery(id+"F1.wireOp",EDGE,"E3")])],"isStart":false});
            transform(context, id + "F13", {"entities" : qUnion([Q0]), "transformType" : TransformType.TRANSLATION_ENTITY, "oppositeDirectionEntity" : false, "transformLine" : qUnion([Q1, Q2]), "makeCopy" : true});
        }
        {
            var Q0;
            Q0=makeQuery(id+"F12.opPattern","COPY",BODY,{"derivedFrom":makeQuery(id+"F10.opExtrude","SWEPT_BODY",BODY,{"disambiguationData":[OSD([sQuery(id+"F1.wireOp",EDGE,"E8.2.0.1"),sQuery(id+"F1.wireOp",EDGE,"E8.2.0.4"),sQuery(id+"F9.wireOp",EDGE,"E10")])]}),"instanceName":"1"});
            var Q1;
            Q1=makeQuery(id+"F3.opExtrude","CAP_VERTEX",VERTEX,{"disambiguationData":[OSD([sQuery(id+"F1.wireOp",EDGE,"E8.3.0.1"),sQuery(id+"F1.wireOp",EDGE,"E8.3.0.4")])],"isStart":false});
            var Q2;
            Q2=makeQuery(id+"F3.opExtrude","CAP_VERTEX",VERTEX,{"disambiguationData":[OSD([sQuery(id+"F1.wireOp",EDGE,"E8.4.0.1"),sQuery(id+"F1.wireOp",EDGE,"E8.4.0.4")])],"isStart":false});
            transform(context, id + "F14", {"entities" : qUnion([Q0]), "transformType" : TransformType.TRANSLATION_ENTITY, "oppositeDirectionEntity" : false, "transformLine" : qUnion([Q1, Q2]), "makeCopy" : true});
        }
        {
            var Q0;
            {var subQ0=sQuery(id+"F4.wireOp",EDGE,"E9.bottom");var subQ1=sQuery(id+"F1.wireOp",EDGE,"E0");Q0=makeQuery(id+"F5.boolean.opBoolean","COPY",EDGE,{"derivedFrom":makeQuery(id+"F5.opExtrude","SWEPT_EDGE",EDGE,{"disambiguationData":[OSD([subQ1,subQ0]),TDD([makeQuery(id+"F4.imprint","INTERSECT",VERTEX,{"disambiguationData":[OD(1.0)],"derivedFrom":[makeQuery(id+"F3.opExtrude","CAP_EDGE",EDGE,{"disambiguationData":[OSD([subQ1])],"isStart":false}),subQ0]})])]})});}
            var Q1;
            {var subQ0=sQuery(id+"F4.wireOp",EDGE,"E9.bottom");var subQ1=sQuery(id+"F1.wireOp",EDGE,"E8.1.0.3");Q1=makeQuery(id+"F5.boolean.opBoolean","COPY",EDGE,{"derivedFrom":makeQuery(id+"F5.opExtrude","SWEPT_EDGE",EDGE,{"disambiguationData":[OSD([subQ1,subQ0]),TDD([makeQuery(id+"F4.imprint","INTERSECT",VERTEX,{"disambiguationData":[OD(1.0)],"derivedFrom":[makeQuery(id+"F3.opExtrude","CAP_EDGE",EDGE,{"disambiguationData":[OSD([subQ1]),TDD([makeQuery(id+"F1.imprint","IMPRINT",EDGE,{"disambiguationData":[TD([[makeQuery(id+"F1.imprint","INTERSECT",VERTEX,{"disambiguationData":[OD(1.0)],"derivedFrom":[sQuery(id+"F1.wireOp",EDGE,"E0"),subQ1]}),-1.0]])],"derivedFrom":subQ1})])],"isStart":false}),subQ0]})])]})});}
            var Q2;
            {var subQ0=sQuery(id+"F4.wireOp",EDGE,"E9.bottom");var subQ1=sQuery(id+"F1.wireOp",EDGE,"E8.1.0.3");Q2=makeQuery(id+"F5.boolean.opBoolean","COPY",EDGE,{"derivedFrom":makeQuery(id+"F5.opExtrude","SWEPT_EDGE",EDGE,{"disambiguationData":[OSD([subQ1,subQ0]),TDD([makeQuery(id+"F4.imprint","INTERSECT",VERTEX,{"disambiguationData":[OD(0.0)],"derivedFrom":[makeQuery(id+"F3.opExtrude","CAP_EDGE",EDGE,{"disambiguationData":[OSD([subQ1]),TDD([makeQuery(id+"F1.imprint","IMPRINT",EDGE,{"disambiguationData":[TD([[makeQuery(id+"F1.imprint","INTERSECT",VERTEX,{"disambiguationData":[OD(1.0)],"derivedFrom":[sQuery(id+"F1.wireOp",EDGE,"E0"),subQ1]}),-1.0]])],"derivedFrom":subQ1})])],"isStart":false}),subQ0]})])]})});}
            var Q3;
            {var subQ0=sQuery(id+"F4.wireOp",EDGE,"E9.bottom");var subQ1=sQuery(id+"F1.wireOp",EDGE,"E8.2.0.3");Q3=makeQuery(id+"F5.boolean.opBoolean","COPY",EDGE,{"derivedFrom":makeQuery(id+"F5.opExtrude","SWEPT_EDGE",EDGE,{"disambiguationData":[OSD([subQ1,subQ0]),TDD([makeQuery(id+"F4.imprint","INTERSECT",VERTEX,{"disambiguationData":[OD(1.0)],"derivedFrom":[makeQuery(id+"F3.opExtrude","CAP_EDGE",EDGE,{"disambiguationData":[OSD([subQ1]),TDD([makeQuery(id+"F1.imprint","IMPRINT",EDGE,{"disambiguationData":[TD([[makeQuery(id+"F1.imprint","INTERSECT",VERTEX,{"disambiguationData":[OD(1.0)],"derivedFrom":[sQuery(id+"F1.wireOp",EDGE,"E8.1.0.3"),subQ1]}),-1.0]])],"derivedFrom":subQ1})])],"isStart":false}),subQ0]})])]})});}
            var Q4;
            {var subQ0=sQuery(id+"F4.wireOp",EDGE,"E9.bottom");var subQ1=sQuery(id+"F1.wireOp",EDGE,"E8.2.0.3");Q4=makeQuery(id+"F5.boolean.opBoolean","COPY",EDGE,{"derivedFrom":makeQuery(id+"F5.opExtrude","SWEPT_EDGE",EDGE,{"disambiguationData":[OSD([subQ1,subQ0]),TDD([makeQuery(id+"F4.imprint","INTERSECT",VERTEX,{"disambiguationData":[OD(0.0)],"derivedFrom":[makeQuery(id+"F3.opExtrude","CAP_EDGE",EDGE,{"disambiguationData":[OSD([subQ1]),TDD([makeQuery(id+"F1.imprint","IMPRINT",EDGE,{"disambiguationData":[TD([[makeQuery(id+"F1.imprint","INTERSECT",VERTEX,{"disambiguationData":[OD(1.0)],"derivedFrom":[sQuery(id+"F1.wireOp",EDGE,"E8.1.0.3"),subQ1]}),-1.0]])],"derivedFrom":subQ1})])],"isStart":false}),subQ0]})])]})});}
            var Q5;
            {var subQ0=sQuery(id+"F4.wireOp",EDGE,"E9.bottom");var subQ1=sQuery(id+"F1.wireOp",EDGE,"E8.3.0.3");Q5=makeQuery(id+"F5.boolean.opBoolean","COPY",EDGE,{"derivedFrom":makeQuery(id+"F5.opExtrude","SWEPT_EDGE",EDGE,{"disambiguationData":[OSD([subQ1,subQ0]),TDD([makeQuery(id+"F4.imprint","INTERSECT",VERTEX,{"disambiguationData":[OD(1.0)],"derivedFrom":[makeQuery(id+"F3.opExtrude","CAP_EDGE",EDGE,{"disambiguationData":[OSD([subQ1]),TDD([makeQuery(id+"F1.imprint","IMPRINT",EDGE,{"disambiguationData":[TD([[makeQuery(id+"F1.imprint","INTERSECT",VERTEX,{"disambiguationData":[OD(1.0)],"derivedFrom":[sQuery(id+"F1.wireOp",EDGE,"E8.2.0.3"),subQ1]}),-1.0]])],"derivedFrom":subQ1})])],"isStart":false}),subQ0]})])]})});}
            var Q6;
            {var subQ0=sQuery(id+"F4.wireOp",EDGE,"E9.bottom");var subQ1=sQuery(id+"F1.wireOp",EDGE,"E8.4.0.3");Q6=makeQuery(id+"F5.boolean.opBoolean","COPY",EDGE,{"derivedFrom":makeQuery(id+"F5.opExtrude","SWEPT_EDGE",EDGE,{"disambiguationData":[OSD([subQ1,subQ0]),TDD([makeQuery(id+"F4.imprint","INTERSECT",VERTEX,{"disambiguationData":[OD(1.0)],"derivedFrom":[makeQuery(id+"F3.opExtrude","CAP_EDGE",EDGE,{"disambiguationData":[OSD([subQ1])],"isStart":false}),subQ0]})])]})});}
            var Q7;
            {var subQ0=sQuery(id+"F4.wireOp",EDGE,"E9.bottom");var subQ1=sQuery(id+"F1.wireOp",EDGE,"E8.3.0.3");Q7=makeQuery(id+"F5.boolean.opBoolean","COPY",EDGE,{"derivedFrom":makeQuery(id+"F5.opExtrude","SWEPT_EDGE",EDGE,{"disambiguationData":[OSD([subQ1,subQ0]),TDD([makeQuery(id+"F4.imprint","INTERSECT",VERTEX,{"disambiguationData":[OD(0.0)],"derivedFrom":[makeQuery(id+"F3.opExtrude","CAP_EDGE",EDGE,{"disambiguationData":[OSD([subQ1]),TDD([makeQuery(id+"F1.imprint","IMPRINT",EDGE,{"disambiguationData":[TD([[makeQuery(id+"F1.imprint","INTERSECT",VERTEX,{"disambiguationData":[OD(1.0)],"derivedFrom":[sQuery(id+"F1.wireOp",EDGE,"E8.2.0.3"),subQ1]}),-1.0]])],"derivedFrom":subQ1})])],"isStart":false}),subQ0]})])]})});}
            fillet(context, id + "F15", {"entities" : qUnion([Q0, Q1, Q2, Q3, Q4, Q5, Q6, Q7]), "radius" : 5 * mm, "tangentPropagation" : true, "allowEdgeOverflow" : false});
        }
    });
